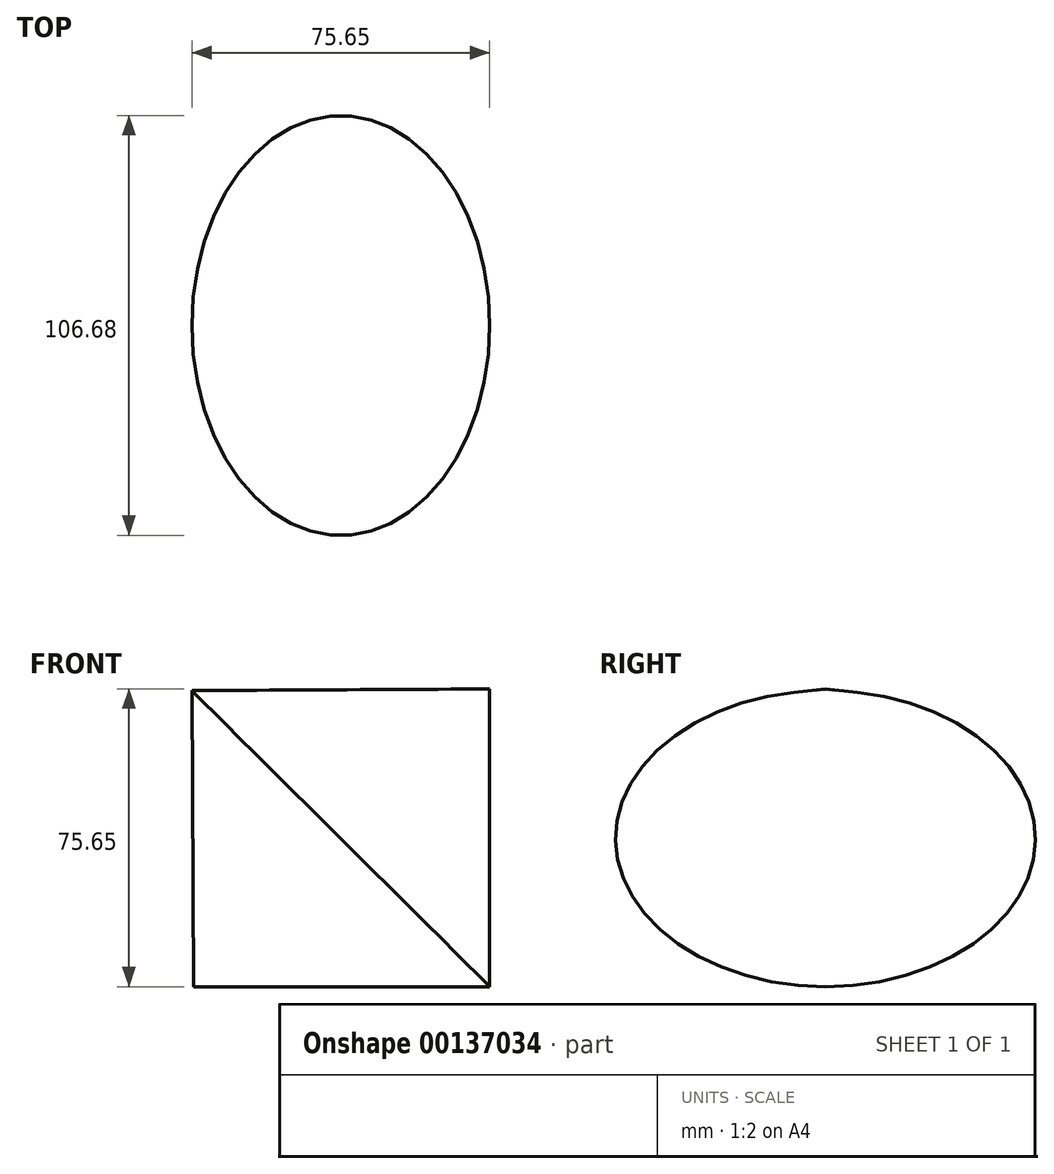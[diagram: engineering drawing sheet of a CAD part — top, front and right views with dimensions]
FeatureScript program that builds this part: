
annotation { "Feature Type Name" : "Feature", "Feature Type Description" : "" }
export const myFeature = defineFeature(function(context is Context, id is Id, definition is map)
    precondition{}
    {
        {
            var Q0;
            Q0=qCreatedBy(makeId("Front.planeOp"),FACE);
            var sketch = newSketch(context, id + "F0", { "sketchPlane" : qUnion([Q0])});
            skLineSegment(sketch, "E0", {"start": v(0, 75.65) * mm, "end": v(-75.22, 0) * mm});
            skLineSegment(sketch, "E1", {"start": v(-75.22, 0) * mm, "end": v(0, 0) * mm});
            skLineSegment(sketch, "E2", {"start": v(0, -1.02) * mm, "end": v(0, 75.65) * mm});
            skSolve(sketch);
        }
        {
            var Q0;
            {var subQ0=sQuery(id+"F0.wireOp",EDGE,"E0");Q0=makeQuery(id+"F0.imprint","IMPRINT",FACE,{"disambiguationData":[TD([[makeQuery(id+"F0.imprint","IMPRINT",EDGE,{"derivedFrom":subQ0}),1.0]])]});}
            var Q1;
            Q1=sQuery(id+"F0.wireOp",EDGE,"E0");
            revolve(context, id + "F1", {"entities" : qUnion([Q0]), "axis" : qUnion([Q1]), "revolveType" : RevolveType.FULL});
        }
    });
